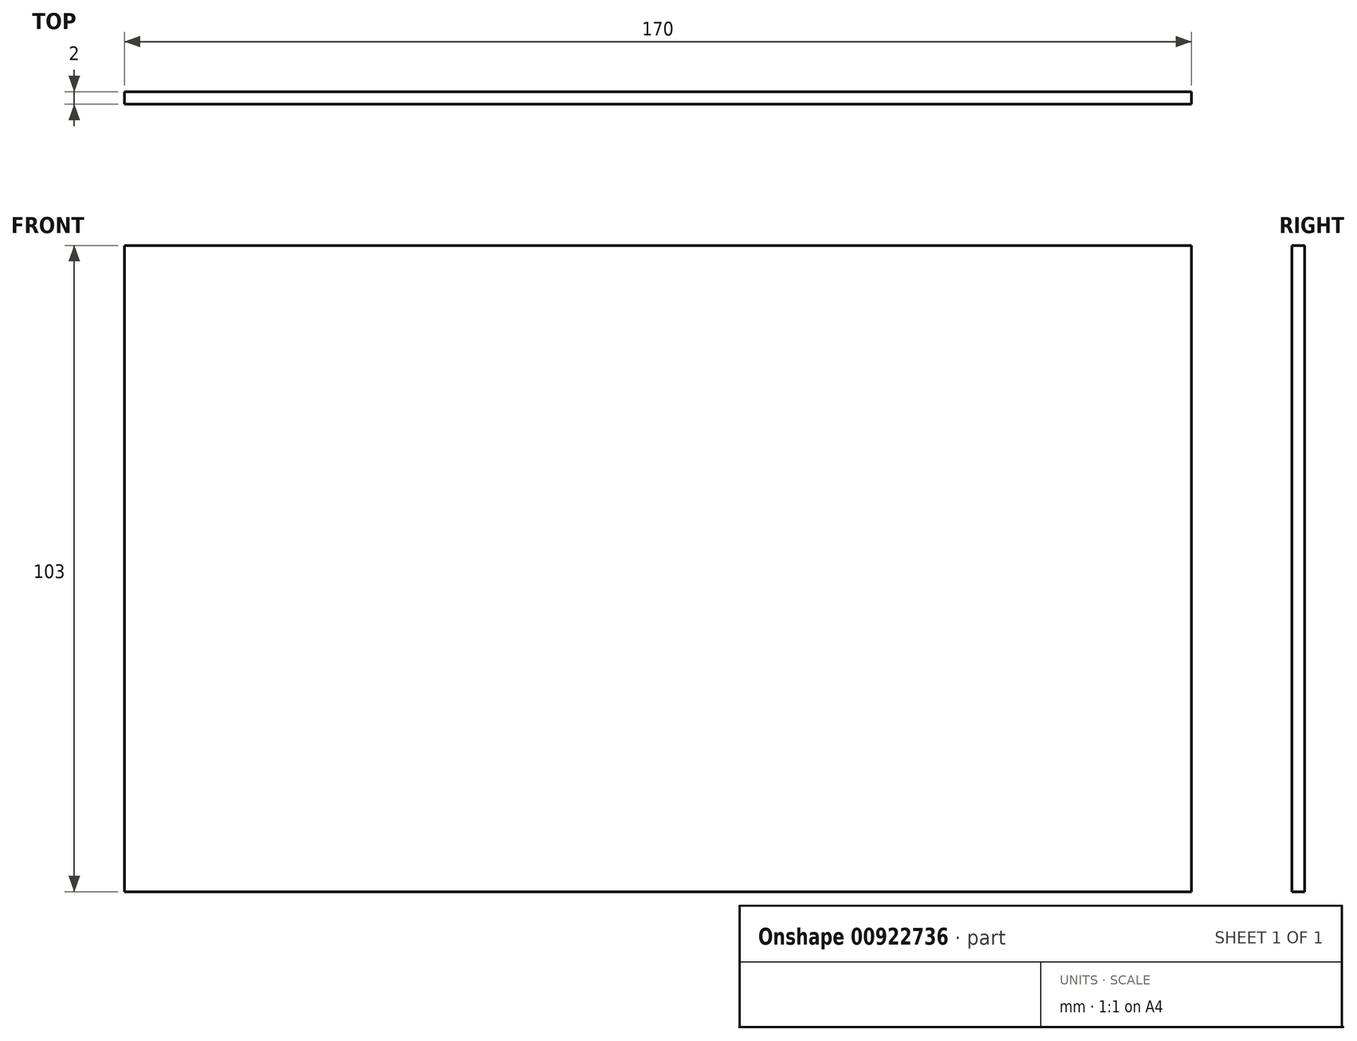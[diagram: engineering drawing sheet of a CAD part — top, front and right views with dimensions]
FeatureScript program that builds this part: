
annotation { "Feature Type Name" : "Feature", "Feature Type Description" : "" }
export const myFeature = defineFeature(function(context is Context, id is Id, definition is map)
    precondition{}
    {
        {
            var Q0;
            Q0=qCreatedBy(makeId("Front.planeOp"),FACE);
            var sketch = newSketch(context, id + "F0", { "sketchPlane" : qUnion([Q0])});
            skLineSegment(sketch, "E0.bottom", {"start": v(87, -51.5) * mm, "end": v(-87, -51.5) * mm});
            skLineSegment(sketch, "E0.top", {"start": v(87, 51.5) * mm, "end": v(-87, 51.5) * mm});
            skLineSegment(sketch, "E0.left", {"start": v(87, -51.5) * mm, "end": v(87, 51.5) * mm});
            skLineSegment(sketch, "E0.right", {"start": v(-87, -51.5) * mm, "end": v(-87, 51.5) * mm});
            skPoint(sketch, "E0.middle", {"position": v(0, 0) * mm});
            skLineSegment(sketch, "E1.bottom", {"start": v(-87, 51.5) * mm, "end": v(-85, 51.5) * mm});
            skLineSegment(sketch, "E1.top", {"start": v(-87, -51.5) * mm, "end": v(-85, -51.5) * mm});
            skLineSegment(sketch, "E1.left", {"start": v(-87, 51.5) * mm, "end": v(-87, -51.5) * mm});
            skLineSegment(sketch, "E1.right", {"start": v(-85, 51.5) * mm, "end": v(-85, -51.5) * mm});
            skLineSegment(sketch, "E2.bottom", {"start": v(87, 51.5) * mm, "end": v(85, 51.5) * mm});
            skLineSegment(sketch, "E2.top", {"start": v(87, -51.5) * mm, "end": v(85, -51.5) * mm});
            skLineSegment(sketch, "E2.left", {"start": v(87, 51.5) * mm, "end": v(87, -51.5) * mm});
            skLineSegment(sketch, "E2.right", {"start": v(85, 51.5) * mm, "end": v(85, -51.5) * mm});
            skLineSegment(sketch, "E3.bottom", {"start": v(-87, -51.5) * mm, "end": v(87, -51.5) * mm});
            skLineSegment(sketch, "E3.top", {"start": v(-87, -49.5) * mm, "end": v(87, -49.5) * mm});
            skLineSegment(sketch, "E3.left", {"start": v(-87, -51.5) * mm, "end": v(-87, -49.5) * mm});
            skLineSegment(sketch, "E3.right", {"start": v(87, -51.5) * mm, "end": v(87, -49.5) * mm});
            skSolve(sketch);
        }
        {
            var Q0;
            {var subQ0=sQuery(id+"F0.wireOp",EDGE,"E1.bottom");Q0=makeQuery(id+"F0.imprint","IMPRINT",FACE,{"disambiguationData":[TD([[makeQuery(id+"F0.imprint","IMPRINT",EDGE,{"derivedFrom":subQ0}),-1.0]])]});}
            var Q1;
            {var subQ5=sQuery(id+"F0.wireOp",EDGE,"E3.left");Q1=makeQuery(id+"F0.imprint","IMPRINT",FACE,{"disambiguationData":[TD([[makeQuery(id+"F0.imprint","IMPRINT",EDGE,{"derivedFrom":subQ5}),-1.0]])]});}
            var Q2;
            {var subQ0=sQuery(id+"F0.wireOp",EDGE,"E3.bottom");var subQ1=sQuery(id+"F0.wireOp",EDGE,"E1.right");var subQ2=makeQuery(id+"F0.imprint","INTERSECT",VERTEX,{"derivedFrom":[subQ1,subQ0]});Q2=makeQuery(id+"F0.imprint","IMPRINT",FACE,{"disambiguationData":[TD([[makeQuery(id+"F0.imprint","IMPRINT",EDGE,{"disambiguationData":[TD([[subQ2,1.0]])],"derivedFrom":subQ1}),1.0]])]});}
            var Q3;
            {var subQ5=sQuery(id+"F0.wireOp",EDGE,"E3.right");Q3=makeQuery(id+"F0.imprint","IMPRINT",FACE,{"disambiguationData":[TD([[makeQuery(id+"F0.imprint","IMPRINT",EDGE,{"derivedFrom":subQ5}),1.0]])]});}
            var Q4;
            {var subQ0=sQuery(id+"F0.wireOp",EDGE,"E2.bottom");Q4=makeQuery(id+"F0.imprint","IMPRINT",FACE,{"disambiguationData":[TD([[makeQuery(id+"F0.imprint","IMPRINT",EDGE,{"derivedFrom":subQ0}),1.0]])]});}
            extrude(context, id + "F1", {"entities" : qUnion([Q0, Q1, Q2, Q3, Q4]), "endBound" : BoundingType.SYMMETRIC, "depth" : 2 * mm, "offsetDistance" : 25 * mm});
        }
    });
